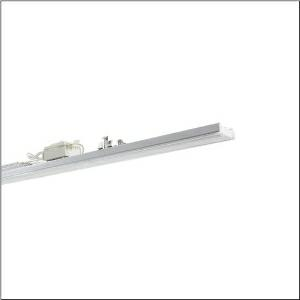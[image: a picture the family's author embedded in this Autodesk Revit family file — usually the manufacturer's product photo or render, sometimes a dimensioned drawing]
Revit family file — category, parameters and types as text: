
# Revit family: licross_r__11_recessed_mo_51tl12dv4fxg_26c5
name_source: partatom
category: Lighting Fixtures
units: mm (PartAtom-declared; Revit-internal decimal feet)

## family parameters
Cut with Voids When Loaded = No
Host = Face
Light Source = No
Part Type = Normal
Room Calculation Point = No
Round Connector Dimension = Use Diameter
Shared = No

## types (1)
- --- (1 x LED, 15360 lm, 84.1 W, 4000K)
    Apparent Load = 84 VA
    CIE Flux Codes = 67 92 99 100 100
    Color Rendering = 80
    Color Temperature = 4000K
    Default Elevation = 1800 mm
    Description = Licross® 11 Recessed MO, luminaire insert, of sheet steel, coil coated, white, length: 2.250mm, width: 66mm, height: 67mm, LED rated luminous flux: 15.360lm, light colour: 840, control gear: DALI 2, with plug, 5-pole, with phase selection, mains connection: 220..240V, AC, 50/60Hz, rated input power: 84W, halogen-free wiring, primary optical cover: cover, of PMMA, light emission: direct distribution, primary light characteristic: symmetric, protection rating (complete): IP40, insulation class (complete): insulation class I (protective earthing), certification: CE, ENEC, VDE, UKCA, protection symbol: D if used in an environment without relevant dust loads with corresponding accessories, impact resistance: IK06, permissible ambient temperature for indoor applications: -25..+35°C, corresponds to IFS (International Featured Standards) requirements for safety and quality in the food industry, reducing of maximum allowable ambient temperature of 5°C with ceiling mounting, LABS conformity tested according to VDMA 24364:2018-05, packaging unit: 1 piece
    Height = 58 mm
    Lamp = 1 x LED
    Lamp Light Flux = 15360 lm
    Lamp Power = 84.1 W
    Lamp count = 1
    Length = 2250 mm
    Luminous efficacy = 183 lm/W
    Manufacturer = Siteco
    ModVariant = No
    Model = 51TL12DV4FXG
    Mounting Place = Ceiling
    Mounting Type = Pendant
    Number of Poles = 1
    OnlyDefault = Yes
    Power Factor = 1
    Product Name = Licross® 11 Recessed MO
    Product group = luminaire insert
    ProductGroupID = 902
    Protection Class = Protection class I
    Protection Degree = IP 40
    RLX_Detail_Level = 1
    RLX_Emergency_Light_Flux = 0 lm
    RLX_Emergency_Type = 0
    RLX_Emergency_Type_DB = No
    RlxData = <blob elided: 29437 chars, md5=a3cd6432>
    Socket = socket
    Standby Power = 0 W
    System Light Flux = 15360 lm
    System Power = 84 W
    Type Comments = factory setting: luminous flux: 100 % | dim-lin: 254 | 378 mA
    Type Image = l_1296930.jpg
    URL = http://relux.com
    VarID = @adj_100434
    Voltage = 0 V
    Weight = 0.00 kg
    Width = 66 mm

## geometry (parser evidence)
native form markers: Blend x4, Sweep x10
no freeform markers — native parametric forms only
